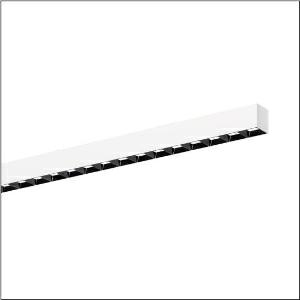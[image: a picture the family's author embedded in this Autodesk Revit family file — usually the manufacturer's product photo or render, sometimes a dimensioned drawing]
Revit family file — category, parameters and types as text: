
# Revit family: silica_r__21_51mx24tat4w_113b
name_source: partatom
category: Lighting Fixtures
units: mm (PartAtom-declared; Revit-internal decimal feet)

## family parameters
Cut with Voids When Loaded = No
Host = Face
Light Source = No
Part Type = Normal
Room Calculation Point = No
Round Connector Dimension = Use Diameter
Shared = No

## types (1)
- --- (1 x LED, 3280 lm, 32.4 W, 6500K)
    Apparent Load = 32 VA
    CIE Flux Codes = 74 94 99 100 100
    Color Rendering = 80
    Color Temperature = 6500K
    Default Elevation = 1800 mm
    Description = Silica® 21, office luminaire, primary light control with darklight reflector, of PMMA, black, light emission: direct distribution, primary light characteristic: asymmetric, installation type: surface-mounted, LED, rated luminous flux: 3.280lm, luminous efficacy: 96lm/W, light colour: 8tw, colour temperature: 2700..6500K, control gear: ECG DALI, with terminal, 3+2-pole, max. 2.5mm², mains connection: 220..240V, AC, 50/60Hz, rated input power: 34.1W, luminaire housing, of aluminium, traffic white (RAL 9016), length: 1.204mm, width: 53mm, height: 53mm, protection rating (complete): IP20, insulation class (complete): insulation class I (protective earthing), certification: CE, permissible operating ambient temperature: 0..+35°C, standard: EN 50419, packaging unit: 1 piece
    Height = 0 mm  [stored 0 ft]
    Lamp = 1 x LED
    Lamp Light Flux = 3280 lm
    Lamp Power = 32.4 W
    Lamp count = 1
    Length = 1204 mm
    Luminous efficacy = 101 lm/W
    Manufacturer = Siteco
    ModVariant = No
    Model = 51MX24TAT4W
    Mounting Place = Ceiling
    Mounting Type = Recessed
    Number of Poles = 1
    OnlyDefault = Yes
    Power Factor = 1
    Product Name = Silica® 21
    Product group = office luminaire | ceiling recessed
    ProductGroupID = 401
    Protection Class = Protection class I
    Protection Degree = IP 20
    RLX_Detail_Level = 1
    RLX_Emergency_Light_Flux = 0 lm
    RLX_Emergency_Type = 0
    RLX_Emergency_Type_DB = No
    RlxData = <blob elided: 38221 chars, md5=94a52b5e>
    Socket = socket
    Standby Power = 0 W
    System Light Flux = 3280 lm
    System Power = 32 W
    Type Comments = individual setting
    Type Image = l_1313592.jpg
    URL = http://relux.com
    VarID = @adj_089385
    Voltage = 0 V
    Weight = 0.00 kg
    Width = 53 mm

note: [stored X ft] marks values corroborated as IEEE doubles in the binary element streams (Revit-internal decimal feet)

## geometry (parser evidence)
native form markers: Blend x4, Sweep x11
no freeform markers — native parametric forms only
